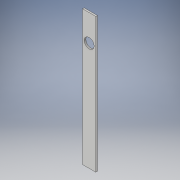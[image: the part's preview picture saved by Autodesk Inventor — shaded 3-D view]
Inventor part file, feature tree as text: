
AUTODESK INVENTOR PART (.ipt)
format: ipt  version: 2018 (Build 220112000, 112)  size: 98,304 bytes
history: native  units: in
note: dims shown in document units (in); Inventor stores cm internally (conversion verified against a paired STEP export)
features: extrude x1, sketch x1
ambient origin geometry x8: Origin, YZ Plane, XZ Plane, XY Plane, X Axis, Y Axis, Z Axis, Center Point
bodies: Solid1 (feature_tree)
feature tree (2):
  extrude  "Extrusion1"  Depth=10.1875in
  sketch  "Sketch1"  dims[d0=1.0in d1=10.1875in d2=8.1875in d3=0.75in d4=0.125in d5=0.0in]
